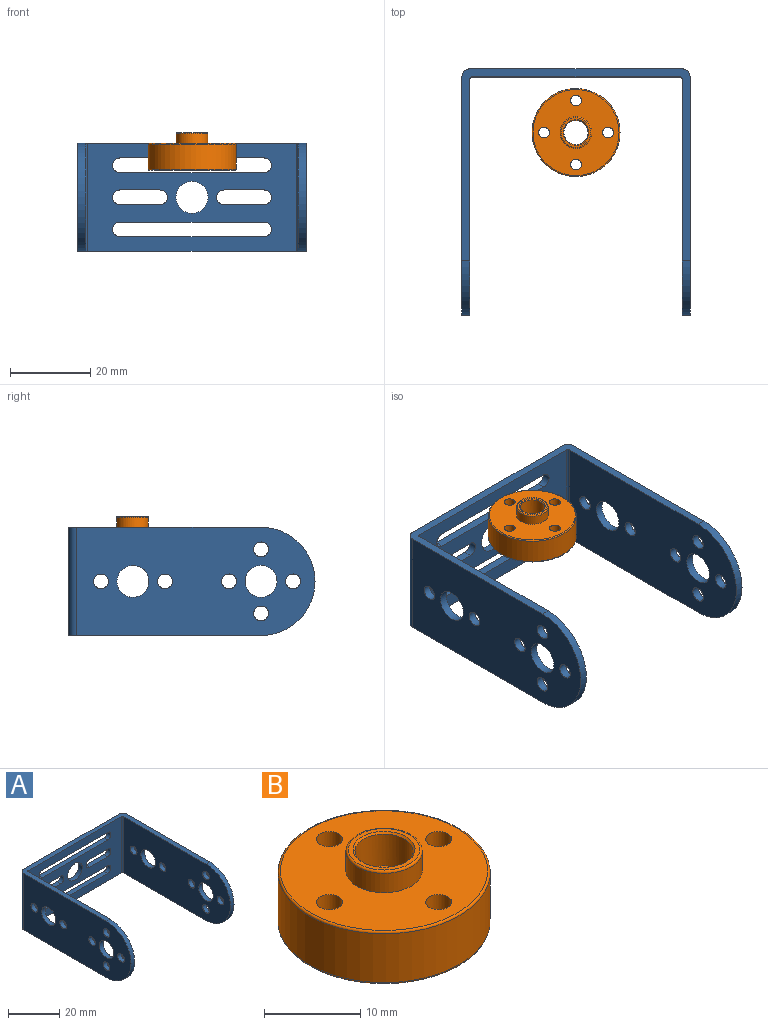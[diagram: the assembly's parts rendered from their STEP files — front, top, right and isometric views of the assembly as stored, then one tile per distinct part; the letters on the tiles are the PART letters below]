
ASSEMBLY  parts=2 mates=1
PART A: 47 faces, bbox 57x61.5x27 mm
  f0: cylinder r=1.85mm len=3.7mm, axis (1,0,0), area 23.2mm2, adj f19,f20
  f1: cylinder r=1.85mm len=3.7mm, axis (1,0,0), area 23.2mm2, adj f17,f22
  f2: cylinder r=1.85mm len=3.7mm, axis (1,0,0), area 23.2mm2, adj f19,f20
  f3: cylinder r=1.85mm len=3.7mm, axis (1,0,0), area 23.2mm2, adj f17,f22
  f4: cylinder r=4mm len=8mm, axis (1,0,0), area 50.3mm2, adj f19,f20
  f5: cylinder r=4mm len=8mm, axis (1,0,0), area 50.3mm2, adj f17,f22
  f6: cylinder r=1.85mm len=3.7mm, axis (-1,0,0), area 23.2mm2, adj f19,f20
  f7: cylinder r=1.85mm len=3.7mm, axis (-1,0,0), area 23.2mm2, adj f17,f22
  f8: cylinder r=1.85mm len=3.7mm, axis (-1,0,0), area 23.2mm2, adj f19,f20
  f9: cylinder r=1.85mm len=3.7mm, axis (-1,0,0), area 23.2mm2, adj f17,f22
  f10: cylinder r=1.85mm len=3.7mm, axis (-1,0,0), area 23.2mm2, adj f19,f20
  f11: cylinder r=1.85mm len=3.7mm, axis (-1,0,0), area 23.2mm2, adj f17,f22
  f12: cylinder r=1.85mm len=3.7mm, axis (-1,0,0), area 23.2mm2, adj f19,f20
  f13: cylinder r=1.85mm len=3.7mm, axis (-1,0,0), area 23.2mm2, adj f17,f22
  f14: cylinder r=4mm len=8mm, axis (-1,0,0), area 50.3mm2, adj f19,f20
  f15: cylinder r=4mm len=8mm, axis (-1,0,0), area 50.3mm2, adj f17,f22
  f16: cylinder r=4mm len=8mm, axis (0,1,0), area 50.3mm2, adj f18,f21
  f17: plane 59.5x27mm, normal (1,0,0), area 1363.2mm2, adj f1,f3,f5,f7,f9,f11,f13,f15
  f18: plane 53x27mm, normal (0,1,0), area 997.3mm2, adj f16,f23,f24,f25,f26,f27,f28,f29
  f19: plane 59.5x27mm, normal (-1,0,0), area 1363.2mm2, adj f0,f2,f4,f6,f8,f10,f12,f14
  f20: plane 59x27mm, normal (1,0,0), area 1349.7mm2, adj f0,f2,f4,f6,f8,f10,f12,f14
  f21: plane 52x27mm, normal (0,-1,0), area 970.3mm2, adj f16,f23,f24,f25,f26,f27,f28,f29
  f22: plane 59x27mm, normal (-1,0,0), area 1349.7mm2, adj f1,f3,f5,f7,f9,f11,f13,f15
  f23: plane 57x48mm, normal (0,0,1), area 296.4mm2, adj f17,f18,f19,f20,f21,f22,f41,f42
  f24: plane 57x48mm, normal (0,0,-1), area 296.4mm2, adj f17,f18,f19,f20,f21,f22,f41,f42
  f25: cylinder r=1.85mm len=3.7mm, axis (0,1,0), area 11.6mm2, adj f18,f21,f26,f28
  f26: plane 36x2mm, normal (0,0,1), area 72mm2, adj f18,f21,f25,f27
  f27: cylinder r=1.85mm len=3.7mm, axis (0,1,0), area 11.6mm2, adj f18,f21,f26,f28
  f28: plane 36x2mm, normal (0,0,-1), area 72mm2, adj f18,f21,f25,f27
  f29: cylinder r=1.85mm len=3.7mm, axis (0,1,0), area 11.6mm2, adj f18,f21,f30,f32
  f30: plane 36x2mm, normal (0,0,1), area 72mm2, adj f18,f21,f29,f31
  f31: cylinder r=1.85mm len=3.7mm, axis (0,1,0), area 11.6mm2, adj f18,f21,f30,f32
  f32: plane 36x2mm, normal (0,0,-1), area 72mm2, adj f18,f21,f29,f31
  f33: cylinder r=1.85mm len=3.7mm, axis (0,1,0), area 11.6mm2, adj f18,f21,f34,f36
  f34: plane 10x2mm, normal (0,0,-1), area 20mm2, adj f18,f21,f33,f35
  f35: cylinder r=1.85mm len=3.7mm, axis (0,1,0), area 11.6mm2, adj f18,f21,f34,f36
  f36: plane 10x2mm, normal (0,0,1), area 20mm2, adj f18,f21,f33,f35
  f37: cylinder r=1.85mm len=3.7mm, axis (0,1,0), area 11.6mm2, adj f18,f21,f38,f40
  f38: plane 10x2mm, normal (0,0,1), area 20mm2, adj f18,f21,f37,f39
  f39: cylinder r=1.85mm len=3.7mm, axis (0,1,0), area 11.6mm2, adj f18,f21,f38,f40
  f40: plane 10x2mm, normal (0,0,-1), area 20mm2, adj f18,f21,f37,f39
  f41: cylinder r=13.5mm len=27mm, axis (1,0,0), area 84.8mm2, adj f17,f22,f23,f24
  f42: cylinder r=13.5mm len=27mm, axis (-1,0,0), area 84.8mm2, adj f19,f20,f23,f24
  f43: cylinder r=2mm len=27mm, axis (0,0,-1), area 84.8mm2, adj f18,f19,f23,f24
  f44: cylinder r=2mm len=27mm, axis (0,0,-1), area 84.8mm2, adj f17,f18,f23,f24
  f45: cylinder r=0.5mm len=27mm, axis (0,0,1), area 21.2mm2, adj f21,f22,f23,f24
  f46: cylinder r=0.5mm len=27mm, axis (0,0,1), area 21.2mm2, adj f20,f21,f23,f24
PART B: 16 faces, bbox 23.8x23.8x9.4 mm
  f0: torus R=3.71mm, axis (0,0,1), area 9.6mm2, adj f11,f15
  f1: torus R=10.75mm, axis (0,0,1), area 26.9mm2, adj f12,f13
  f2: torus R=10.75mm, axis (0,0,1), area 26.9mm2, adj f12,f14
  f3: cone r=3.01mm half-angle=45deg, axis (0,0,1), area 5.5mm2, adj f10,f15
  f4: cone r=3.21mm half-angle=45deg, axis (0,0,-1), area 5.5mm2, adj f10,f14
  f5: cylinder r=2mm len=8.88mm, axis (-0.71,-0.71,0), area 107.6mm2, adj f10,f12
  f6: cylinder r=1.35mm len=6.7mm, axis (0,0,1), area 56.8mm2, adj f13,f14
  f7: cylinder r=1.35mm len=6.7mm, axis (0,0,1), area 56.8mm2, adj f13,f14
  f8: cylinder r=1.35mm len=6.7mm, axis (0,0,1), area 56.8mm2, adj f13,f14
  f9: cylinder r=1.35mm len=6.7mm, axis (0,0,1), area 56.8mm2, adj f13,f14
  f10: cylinder r=3.01mm len=9mm, axis (0,0,1), area 157.1mm2, adj f3,f4,f5
  f11: cylinder r=3.96mm len=7.93mm, axis (0,0,-1), area 61mm2, adj f0,f13
  f12: cylinder r=11mm len=22mm, axis (0,0,1), area 415.9mm2, adj f1,f2,f5
  f13: plane 21.5x21.5mm, normal (0,0,1), area 290.8mm2, adj f1,f6,f7,f8,f9,f11
  f14: plane 21.5x21.5mm, normal (0,0,-1), area 307.7mm2, adj f2,f4,f6,f7,f8,f9
  f15: plane 7.43x7.43mm, normal (0,0,1), area 10.8mm2, adj f0,f3
PLACE A at identity
PLACE B t=(-2.85,-1.89,-4.65)mm
MATE fastened B.f0 <-> A.f23  axis (0,0,1) through (0,14.85,13.5)mm
